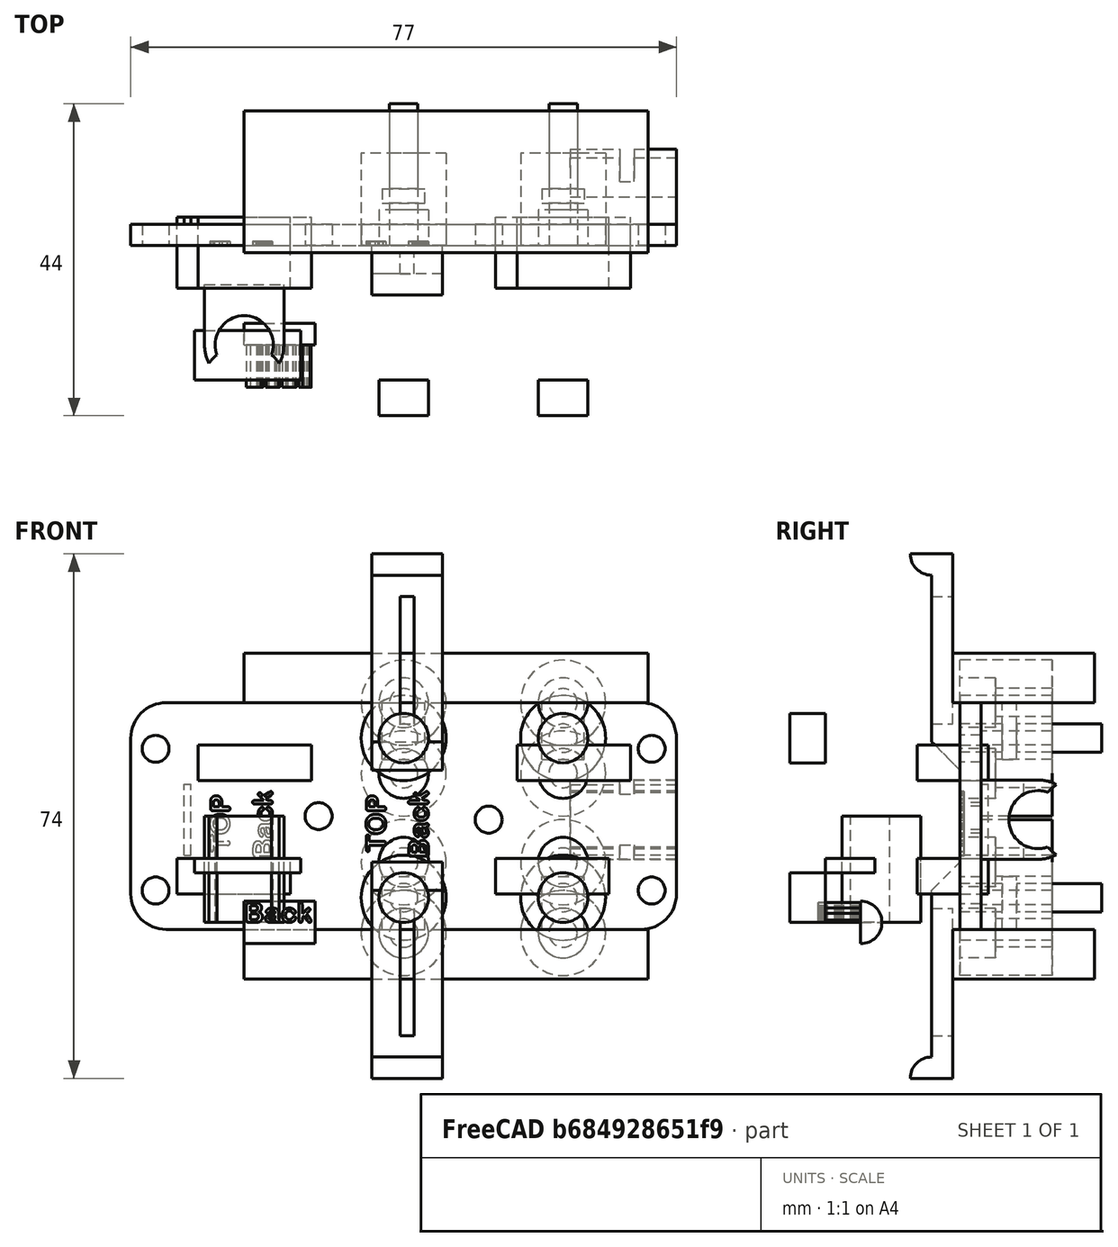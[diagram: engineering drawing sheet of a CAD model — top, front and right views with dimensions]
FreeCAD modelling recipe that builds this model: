
FCSTD DOCUMENT  (FreeCAD 0.16R6712 (Git))
Label: ParkingTransportPlate
License: All rights reserved
LicenseURL: http://en.wikipedia.org/wiki/All_rights_reserved
objects: Part::Cylinder×56, Part::MultiFuse×31, Part::Box×23, Part::Cut×19, Part::Feature×12, Part::Part2DObjectPython×2, Part::Extrusion×1
note: 144 computed .brp shape members not serialized (recipe doc carries the construction recipe); baked Part::Feature solids carry a one-line shape summary decoded from their .brp

FEATURE [Part::Part2DObjectPython] ShapeString002  # Draft 2D object (typed FeaturePython)
  FontFile = <path>
  Size = 3
  String = TOP
  Tracking = 4
FEATURE [Part::Feature] Extrude001002001  label="Extrude001003"
  Placement = pos=(18,0,11) rot=(0,-1,0;1.5708rad)
  shape: bbox 2.835 x 6 x 7.877 mm, 76 faces, 3 solids (baked)
FEATURE [Part::Part2DObjectPython] ShapeString003  # Draft 2D object (typed FeaturePython)
  FontFile = <path>
  Size = 3
  String = Back
  Tracking = 4
FEATURE [Part::Extrusion] Extrude001002002
  Base = -> ShapeString003
  Dir = (0,0,6)
  Placement = pos=(0,0,0) rot=(1,0,0;1.5708rad)
  Solid = false
FEATURE [Part::Feature] Extrude001002002001  label="Extrude001002003"
  Placement = pos=(24,0,10) rot=(0,-1,0;1.5708rad)
  shape: bbox 2.835 x 6 x 9.142 mm, 140 faces, 4 solids (baked)
FEATURE [Part::Box] Box035  label="Würfel034"
  Height = 32
  Length = 77
  Placement = pos=(-16,14,-1) rot=(0,0,1;0rad)
  Width = 3
FEATURE [Part::MultiFuse] Fusion  label="Label"
  Placement = pos=(-20,14.6,-1) rot=(0,0,1;0rad)
  Shapes = -> [Extrude001002002001,Extrude001002001]
FEATURE [Part::Cut] Cut
  Base = -> Box035
  Tool = -> Fusion
FEATURE [Part::Box] Box  label="Würfel"
  Height = 21
  Length = 10
  Placement = pos=(0,0,-2) rot=(0,0,1;0rad)
  Width = 3
FEATURE [Part::Cylinder] Cylinder  label="Zylinder"
  Angle = 180
  Height = 10
  Placement = pos=(0,0,0) rot=(0,1,0;1.5708rad)
  Radius = 3
FEATURE [Part::Feature] Cylinder040  label="Zylinder031"
  Placement = pos=(0,0,-2) rot=(1,0,0;1.5708rad)
  shape: bbox 10 x 6 x 3 mm, 4 faces (baked)
FEATURE [Part::MultiFuse] Fusion026006
  Placement = pos=(18,10,-20) rot=(0,0,1;0rad)
  Shapes = -> [Box,Cylinder040]
FEATURE [Part::Box] Box036  label="Würfel035"
  Height = 21
  Length = 10
  Placement = pos=(0,0,-2) rot=(0,0,1;0rad)
  Width = 3
FEATURE [Part::Feature] Cylinder041  label="Zylinder032"
  Placement = pos=(0,0,-2) rot=(1,0,0;1.5708rad)
  shape: bbox 10 x 6 x 3 mm, 4 faces (baked)
FEATURE [Part::MultiFuse] Fusion026007
  Placement = pos=(28,10,50) rot=(0,1,0;3.14159rad)
  Shapes = -> [Box036,Cylinder041]
FEATURE [Part::Cylinder] Cylinder051  label="Zylinder042"
  Angle = 90
  Height = 40
  Placement = pos=(33,25,29) rot=(1,0,0;1.5708rad)
  Radius = 8
FEATURE [Part::Cylinder] Cylinder052  label="Zylinder043"
  Angle = 90
  Height = 40
  Placement = pos=(33,25,29) rot=(1,0,0;1.5708rad)
  Radius = 5
FEATURE [Part::Cut] Cut011004004
  Base = -> Cylinder051
  Placement = pos=(18,0,-7) rot=(0,-1,0;1.5708rad)
  Tool = -> Cylinder052
FEATURE [Part::Cylinder] Cylinder053  label="Zylinder044"
  Angle = 90
  Height = 40
  Placement = pos=(33,25,29) rot=(1,0,0;1.5708rad)
  Radius = 8
FEATURE [Part::Cylinder] Cylinder054  label="Zylinder045"
  Angle = 90
  Height = 40
  Placement = pos=(33,25,29) rot=(1,0,0;1.5708rad)
  Radius = 5
FEATURE [Part::Cut] Cut011004005
  Base = -> Cylinder053
  Placement = pos=(22,0,33) rot=(0,1,0;3.14159rad)
  Tool = -> Cylinder054
FEATURE [Part::Cylinder] Cylinder055  label="Zylinder046"
  Angle = 90
  Height = 40
  Placement = pos=(33,25,29) rot=(1,0,0;1.5708rad)
  Radius = 8
FEATURE [Part::Cylinder] Cylinder056  label="Zylinder047"
  Angle = 90
  Height = 40
  Placement = pos=(33,25,29) rot=(1,0,0;1.5708rad)
  Radius = 5
FEATURE [Part::Cut] Cut011004006
  Base = -> Cylinder055
  Placement = pos=(23,0,-3) rot=(0,0,1;0rad)
  Tool = -> Cylinder056
FEATURE [Part::Cylinder] Cylinder059  label="Zylinder050"
  Angle = 90
  Height = 40
  Placement = pos=(33,25,29) rot=(1,0,0;1.5708rad)
  Radius = 8
FEATURE [Part::Cylinder] Cylinder060  label="Zylinder051"
  Angle = 90
  Height = 40
  Placement = pos=(33,25,29) rot=(1,0,0;1.5708rad)
  Radius = 5
FEATURE [Part::Cut] Cut011004008
  Base = -> Cylinder059
  Placement = pos=(27,0,37) rot=(0,1,0;1.5708rad)
  Tool = -> Cylinder060
FEATURE [Part::MultiFuse] Fusion026012  label="RoundEdges"
  Shapes = -> [Cut011004008,Cut011004006,Cut011004004,Cut011004005]
FEATURE [Part::Box] Box037  label="Würfel036"
  Height = 10
  Length = 10
  Width = 4
FEATURE [Part::Box] Box038  label="Würfel037"
  Height = 10
  Length = 10
  Placement = pos=(0,-5,9) rot=(-1,0,0;0.785398rad)
  Width = 6
FEATURE [Part::Cut] Cut011004009
  Base = -> Box037
  Placement = pos=(18,10,-1) rot=(0,0,1;0rad)
  Tool = -> Box038
FEATURE [Part::Box] Box039  label="Würfel038"
  Height = 10
  Length = 10
  Width = 4
FEATURE [Part::Box] Box040  label="Würfel039"
  Height = 10
  Length = 10
  Placement = pos=(0,-5,9) rot=(-1,0,0;0.785398rad)
  Width = 6
FEATURE [Part::Cut] Cut011004010
  Base = -> Box039
  Placement = pos=(28,10,31) rot=(0,1,0;3.14159rad)
  Tool = -> Box040
FEATURE [Part::Box] Box041  label="Würfel040"
  Height = 18
  Length = 2
  Placement = pos=(22,-1,-16) rot=(0,0,1;0rad)
  Width = 14
FEATURE [Part::Box] Box042  label="Würfel041"
  Height = 18
  Length = 2
  Placement = pos=(22,-1,28) rot=(0,0,1;0rad)
  Width = 14
FEATURE [Part::MultiFuse] Fusion026013
  Shapes = -> [Fusion026007,Cut011004010]
FEATURE [Part::Cut] Cut011004011  label="DecuplerLeft"
  Base = -> Fusion026013
  Tool = -> Box042
FEATURE [Part::MultiFuse] Fusion026014
  Shapes = -> [Fusion026006,Cut011004009]
FEATURE [Part::Cut] Cut011004012  label="DecuplerRight"
  Base = -> Fusion026014
  Tool = -> Box041
FEATURE [Part::Cylinder] Cylinder034  label="Zylinder025"
  Angle = 360
  Height = 26
  Placement = pos=(-13,16,4.5) rot=(1,0,0;1.5708rad)
  Radius = 1.9
FEATURE [Part::Cylinder] Cylinder035  label="Zylinder026"
  Angle = 360
  Height = 26
  Placement = pos=(-13,16,24.5) rot=(1,0,0;1.5708rad)
  Radius = 1.9
FEATURE [Part::Cylinder] Cylinder036  label="Zylinder027"
  Angle = 360
  Height = 26
  Placement = pos=(10.5,16,15) rot=(1,0,0;1.5708rad)
  Radius = 1.9
FEATURE [Part::MultiFuse] Fusion026003
  Placement = pos=(0.5,0,0) rot=(0,0,1;0rad)
  Shapes = -> [Cylinder034,Cylinder035]
FEATURE [Part::Cylinder] Cylinder037  label="Zylinder028"
  Angle = 360
  Height = 26
  Placement = pos=(-13,16,4.5) rot=(1,0,0;1.5708rad)
  Radius = 1.9
FEATURE [Part::Cylinder] Cylinder038  label="Zylinder029"
  Angle = 360
  Height = 26
  Placement = pos=(-13,16,24.5) rot=(1,0,0;1.5708rad)
  Radius = 1.9
FEATURE [Part::MultiFuse] Fusion026004
  Placement = pos=(70.5,0,0) rot=(0,0,1;0rad)
  Shapes = -> [Cylinder037,Cylinder038]
FEATURE [Part::Cylinder] Cylinder039  label="Zylinder030"
  Angle = 360
  Height = 26
  Placement = pos=(34.5,16,14.5) rot=(1,0,0;1.5708rad)
  Radius = 1.9
FEATURE [Part::MultiFuse] Fusion026005  label="Bohrung"
  Placement = pos=(0,3,0) rot=(0,0,1;0rad)
  Shapes = -> [Cylinder036,Fusion026003,Fusion026004,Cylinder039]
FEATURE [Part::MultiFuse] Fusion026015
  Shapes = -> [Fusion026012,Fusion026005]
FEATURE [Part::Cut] Cut011004013  label="BasePlate"
  Base = -> Cut
  Tool = -> Fusion026015
FEATURE [Part::Box] Box034  label="Würfel033"
  Height = 5
  Length = 16
  Placement = pos=(-9.5,-18,4) rot=(0,0,1;0rad)
  Width = 10
FEATURE [Part::Box] Box043  label="Würfel042"
  Height = 5
  Length = 16
  Placement = pos=(35.5,-18,4) rot=(0,0,1;0rad)
  Width = 10
FEATURE [Part::Box] Box044  label="Würfel043"
  Height = 5
  Length = 16
  Placement = pos=(-6.5,-18,20) rot=(0,0,1;0rad)
  Width = 10
FEATURE [Part::Box] Box045  label="Würfel044"
  Height = 5
  Length = 16
  Placement = pos=(38.5,-18,20) rot=(0,0,1;0rad)
  Width = 10
FEATURE [Part::MultiFuse] Fusion026017  label="SripperHoles"
  Placement = pos=(0,26,0) rot=(0,0,1;0rad)
  Shapes = -> [Box034,Box045,Box043,Box044]
FEATURE [Part::Feature] Cut011004014001  label="BasePlateOpen_export"
  shape: bbox 77 x 3 x 32 mm, 246 faces (baked)
FEATURE [Part::Feature] Cut011004013001  label="BasePlate_export"
  shape: bbox 77 x 3 x 32 mm, 230 faces (baked)
FEATURE [Part::Cylinder] Cylinder061  label="Zylinder052"
  Angle = 360
  Height = 20
  Placement = pos=(-3.5,14,0) rot=(0,0,1;0rad)
  Radius = 2
FEATURE [Part::Cylinder] Cylinder001  label="Zylinder001"
  Angle = 360
  Height = 20
  Placement = pos=(-3.5,36.5,0) rot=(0,0,1;0rad)
  Radius = 2
FEATURE [Part::Cylinder] Cylinder002  label="Zylinder002"
  Angle = 360
  Height = 20
  Placement = pos=(19,14,0) rot=(0,0,1;0rad)
  Radius = 2
FEATURE [Part::Cylinder] Cylinder003  label="Zylinder003"
  Angle = 360
  Height = 20
  Placement = pos=(19,36.5,0) rot=(0,0,1;0rad)
  Radius = 2
FEATURE [Part::MultiFuse] Fusion026018
  Placement = pos=(26,10,-10.5) rot=(1,0,0;1.5708rad)
  Shapes = -> [Cylinder061,Cylinder002,Cylinder003,Cylinder001]
FEATURE [Part::Cylinder] Cylinder062  label="Zylinder053"
  Angle = 360
  Height = 5
  Placement = pos=(-3.5,14,0) rot=(0,0,1;0rad)
  Radius = 3.5
FEATURE [Part::Cylinder] Cylinder063  label="Zylinder054"
  Angle = 360
  Height = 5
  Placement = pos=(-3.5,36.5,0) rot=(0,0,1;0rad)
  Radius = 3.5
FEATURE [Part::Cylinder] Cylinder064  label="Zylinder055"
  Angle = 360
  Height = 5
  Placement = pos=(19,14,0) rot=(0,0,1;0rad)
  Radius = 3.5
FEATURE [Part::Cylinder] Cylinder065  label="Zylinder056"
  Angle = 360
  Height = 5
  Placement = pos=(19,36.5,0) rot=(0,0,1;0rad)
  Radius = 3.5
FEATURE [Part::MultiFuse] Fusion026019
  Placement = pos=(26,-5,-10.5) rot=(1,0,0;1.5708rad)
  Shapes = -> [Cylinder062,Cylinder064,Cylinder065,Cylinder063]
FEATURE [Part::Cylinder] Cylinder066  label="Zylinder057"
  Angle = 360
  Height = 13
  Placement = pos=(-3.5,14,0) rot=(0,0,1;0rad)
  Radius = 6
FEATURE [Part::Cylinder] Cylinder067  label="Zylinder058"
  Angle = 360
  Height = 13
  Placement = pos=(-3.5,36.5,0) rot=(0,0,1;0rad)
  Radius = 6
FEATURE [Part::Cylinder] Cylinder068  label="Zylinder059"
  Angle = 360
  Height = 13
  Placement = pos=(19,14,0) rot=(0,0,1;0rad)
  Radius = 6
FEATURE [Part::Cylinder] Cylinder069  label="Zylinder060"
  Angle = 360
  Height = 13
  Placement = pos=(19,36.5,0) rot=(0,0,1;0rad)
  Radius = 6
FEATURE [Part::MultiFuse] Fusion026020  label="E3DV6Mount_Base"
  Placement = pos=(26,27,-15.5) rot=(1,0,0;1.5708rad)
  Shapes = -> [Cylinder066,Cylinder068,Cylinder069,Cylinder067]
FEATURE [Part::MultiFuse] Fusion026021  label="E3DV6Mount_Bohrung"
  Placement = pos=(0,24,-5) rot=(0,0,1;0rad)
  Shapes = -> [Fusion026018,Fusion026019]
FEATURE [Part::MultiFuse] Fusion026022  label="E3DV6Mount_Full"
  Shapes = -> [Fusion026020,Cut011004013]
FEATURE [Part::Cut] Cut011004014002  label="E3DV6Mount"
  Base = -> Fusion026022
  Tool = -> Fusion026021
FEATURE [Part::Feature] Cut011004014002001  label="E3DV6Mount001"
  shape: bbox 77 x 13 x 38 mm, 252 faces (baked)
FEATURE [Part::Feature] Cut011004014002002  label="E3DV6Mount002"
  shape: bbox 77 x 13 x 38.5 mm, 252 faces (baked)
FEATURE [Part::Feature] Extrude001002002002  label="Extrude001002002004"
  Placement = pos=(18,0,11) rot=(0,-1,0;1.5708rad)
  shape: bbox 2.835 x 6 x 7.877 mm, 76 faces, 3 solids (baked)
FEATURE [Part::Feature] Extrude001002002003  label="Extrude001002002005"
  Placement = pos=(24,0,10) rot=(0,-1,0;1.5708rad)
  shape: bbox 2.835 x 6 x 9.142 mm, 140 faces, 4 solids (baked)
FEATURE [Part::Box] Box046  label="Würfel045"
  Height = 32
  Length = 77
  Placement = pos=(-16,14,-1) rot=(0,0,1;0rad)
  Width = 3
FEATURE [Part::MultiFuse] Fusion026023  label="Label001"
  Placement = pos=(-20,14.6,-1) rot=(0,0,1;0rad)
  Shapes = -> [Extrude001002002003,Extrude001002002002]
FEATURE [Part::Cut] Cut011004014002003
  Base = -> Box046
  Tool = -> Fusion026023
FEATURE [Part::Cylinder] Cylinder070  label="Zylinder061"
  Angle = 90
  Height = 40
  Placement = pos=(33,25,29) rot=(1,0,0;1.5708rad)
  Radius = 8
FEATURE [Part::Cylinder] Cylinder071  label="Zylinder062"
  Angle = 90
  Height = 40
  Placement = pos=(33,25,29) rot=(1,0,0;1.5708rad)
  Radius = 5
FEATURE [Part::Cut] Cut011004014002004
  Base = -> Cylinder070
  Placement = pos=(18,0,-7) rot=(0,-1,0;1.5708rad)
  Tool = -> Cylinder071
FEATURE [Part::Cylinder] Cylinder072  label="Zylinder063"
  Angle = 90
  Height = 40
  Placement = pos=(33,25,29) rot=(1,0,0;1.5708rad)
  Radius = 8
FEATURE [Part::Cylinder] Cylinder073  label="Zylinder064"
  Angle = 90
  Height = 40
  Placement = pos=(33,25,29) rot=(1,0,0;1.5708rad)
  Radius = 5
FEATURE [Part::Cut] Cut011004014002005
  Base = -> Cylinder072
  Placement = pos=(22,0,33) rot=(0,1,0;3.14159rad)
  Tool = -> Cylinder073
FEATURE [Part::Cylinder] Cylinder074  label="Zylinder065"
  Angle = 90
  Height = 40
  Placement = pos=(33,25,29) rot=(1,0,0;1.5708rad)
  Radius = 8
FEATURE [Part::Cylinder] Cylinder075  label="Zylinder066"
  Angle = 90
  Height = 40
  Placement = pos=(33,25,29) rot=(1,0,0;1.5708rad)
  Radius = 5
FEATURE [Part::Cut] Cut011004014002006
  Base = -> Cylinder074
  Placement = pos=(23,0,-3) rot=(0,0,1;0rad)
  Tool = -> Cylinder075
FEATURE [Part::Cylinder] Cylinder076  label="Zylinder067"
  Angle = 90
  Height = 40
  Placement = pos=(33,25,29) rot=(1,0,0;1.5708rad)
  Radius = 8
FEATURE [Part::Cylinder] Cylinder077  label="Zylinder068"
  Angle = 90
  Height = 40
  Placement = pos=(33,25,29) rot=(1,0,0;1.5708rad)
  Radius = 5
FEATURE [Part::Cut] Cut011004014002007
  Base = -> Cylinder076
  Placement = pos=(27,0,37) rot=(0,1,0;1.5708rad)
  Tool = -> Cylinder077
FEATURE [Part::MultiFuse] Fusion026024  label="RoundEdges001"
  Shapes = -> [Cut011004014002007,Cut011004014002006,Cut011004014002004,Cut011004014002005]
FEATURE [Part::Cylinder] Cylinder078  label="Zylinder069"
  Angle = 360
  Height = 26
  Placement = pos=(-13,16,4.5) rot=(1,0,0;1.5708rad)
  Radius = 1.9
FEATURE [Part::Cylinder] Cylinder079  label="Zylinder070"
  Angle = 360
  Height = 26
  Placement = pos=(-13,16,24.5) rot=(1,0,0;1.5708rad)
  Radius = 1.9
FEATURE [Part::Cylinder] Cylinder080  label="Zylinder071"
  Angle = 360
  Height = 26
  Placement = pos=(10.5,16,15) rot=(1,0,0;1.5708rad)
  Radius = 1.9
FEATURE [Part::MultiFuse] Fusion026025
  Placement = pos=(0.5,0,0) rot=(0,0,1;0rad)
  Shapes = -> [Cylinder078,Cylinder079]
FEATURE [Part::Cylinder] Cylinder081  label="Zylinder072"
  Angle = 360
  Height = 26
  Placement = pos=(-13,16,4.5) rot=(1,0,0;1.5708rad)
  Radius = 1.9
FEATURE [Part::Cylinder] Cylinder082  label="Zylinder073"
  Angle = 360
  Height = 26
  Placement = pos=(-13,16,24.5) rot=(1,0,0;1.5708rad)
  Radius = 1.9
FEATURE [Part::MultiFuse] Fusion026026
  Placement = pos=(70.5,0,0) rot=(0,0,1;0rad)
  Shapes = -> [Cylinder081,Cylinder082]
FEATURE [Part::Cylinder] Cylinder083  label="Zylinder074"
  Angle = 360
  Height = 26
  Placement = pos=(34.5,16,14.5) rot=(1,0,0;1.5708rad)
  Radius = 1.9
FEATURE [Part::MultiFuse] Fusion026027  label="Bohrung001"
  Placement = pos=(0,3,0) rot=(0,0,1;0rad)
  Shapes = -> [Cylinder080,Fusion026025,Fusion026026,Cylinder083]
FEATURE [Part::MultiFuse] Fusion026028
  Shapes = -> [Fusion026024,Fusion026027]
FEATURE [Part::Cut] Cut011004014002008  label="BasePlate001"
  Base = -> Cut011004014002003
  Tool = -> Fusion026028
FEATURE [Part::Cylinder] Cylinder084  label="Zylinder075"
  Angle = 360
  Height = 20
  Placement = pos=(-3.5,14,0) rot=(0,0,1;0rad)
  Radius = 2
FEATURE [Part::Cylinder] Cylinder085  label="Zylinder076"
  Angle = 360
  Height = 20
  Placement = pos=(-3.5,36.5,0) rot=(0,0,1;0rad)
  Radius = 2
FEATURE [Part::Cylinder] Cylinder086  label="Zylinder077"
  Angle = 360
  Height = 20
  Placement = pos=(19,14,0) rot=(0,0,1;0rad)
  Radius = 2
FEATURE [Part::Cylinder] Cylinder087  label="Zylinder078"
  Angle = 360
  Height = 20
  Placement = pos=(19,36.5,0) rot=(0,0,1;0rad)
  Radius = 2
FEATURE [Part::MultiFuse] Fusion026029  label="Bohrloch"
  Placement = pos=(26,10,-10.5) rot=(1,0,0;1.5708rad)
  Shapes = -> [Cylinder084,Cylinder086,Cylinder087,Cylinder085]
FEATURE [Part::Cylinder] Cylinder088  label="Zylinder079"
  Angle = 360
  Height = 5
  Placement = pos=(-3.5,14,0) rot=(0,0,1;0rad)
  Radius = 3.5
FEATURE [Part::Cylinder] Cylinder089  label="Zylinder080"
  Angle = 360
  Height = 5
  Placement = pos=(-3.5,36.5,0) rot=(0,0,1;0rad)
  Radius = 3.5
FEATURE [Part::Cylinder] Cylinder090  label="Zylinder081"
  Angle = 360
  Height = 5
  Placement = pos=(19,14,0) rot=(0,0,1;0rad)
  Radius = 3.5
FEATURE [Part::Cylinder] Cylinder091  label="Zylinder082"
  Angle = 360
  Height = 5
  Placement = pos=(19,36.5,0) rot=(0,0,1;0rad)
  Radius = 3.5
FEATURE [Part::MultiFuse] Fusion026030  label="MutterSenke"
  Placement = pos=(26,-5,-10.5) rot=(1,0,0;1.5708rad)
  Shapes = -> [Cylinder088,Cylinder090,Cylinder091,Cylinder089]
FEATURE [Part::Cylinder] Cylinder092  label="Zylinder083"
  Angle = 360
  Height = 13
  Placement = pos=(-3.5,14,0) rot=(0,0,1;0rad)
  Radius = 6
FEATURE [Part::Cylinder] Cylinder093  label="Zylinder084"
  Angle = 360
  Height = 13
  Placement = pos=(-3.5,36.5,0) rot=(0,0,1;0rad)
  Radius = 6
FEATURE [Part::Cylinder] Cylinder094  label="Zylinder085"
  Angle = 360
  Height = 13
  Placement = pos=(19,14,0) rot=(0,0,1;0rad)
  Radius = 6
FEATURE [Part::Cylinder] Cylinder095  label="Zylinder086"
  Angle = 360
  Height = 13
  Placement = pos=(19,36.5,0) rot=(0,0,1;0rad)
  Radius = 6
FEATURE [Part::MultiFuse] Fusion026031  label="E3DV6Mount_Base001"
  Placement = pos=(26,27,-10.5) rot=(1,0,0;1.5708rad)
  Shapes = -> [Cylinder092,Cylinder094,Cylinder095,Cylinder093]
FEATURE [Part::Box] Box047  label="Würfel046"
  Height = 12
  Length = 6
  Placement = pos=(19.5,-4,23) rot=(0,0,1;0rad)
  Width = 2
FEATURE [Part::Box] Box048  label="Würfel047"
  Height = 12
  Length = 6
  Placement = pos=(42,-4,-5.5) rot=(0,0,1;0rad)
  Width = 2
FEATURE [Part::Box] Box049  label="Würfel048"
  Height = 12
  Length = 6
  Placement = pos=(19.5,-4,-5.5) rot=(0,0,1;0rad)
  Width = 2
FEATURE [Part::Box] Box050  label="Würfel049"
  Height = 12
  Length = 6
  Placement = pos=(42,-4,23) rot=(0,0,1;0rad)
  Width = 2
FEATURE [Part::MultiFuse] Fusion026034  label="MutterSchlitz"
  Shapes = -> [Box047,Box048,Box049,Box050]
FEATURE [Part::MultiFuse] Fusion026035  label="Bohrung002"
  Placement = pos=(0,24,0) rot=(0,0,1;0rad)
  Shapes = -> [Fusion026029,Fusion026034]
FEATURE [Part::Box] Box051  label="Würfel050"
  Height = 7
  Length = 57
  Placement = pos=(0,13,-8) rot=(0,0,1;0rad)
  Width = 20
FEATURE [Part::Box] Box052  label="Würfel051"
  Height = 7
  Length = 57
  Placement = pos=(0,13,31) rot=(0,0,1;0rad)
  Width = 20
FEATURE [Part::MultiFuse] Fusion026036  label="SideCut"
  Shapes = -> [Box051,Box052]
FEATURE [Part::MultiFuse] Fusion026037  label="fullCut"
  Shapes = -> [Fusion026035,Fusion026036]
FEATURE [Part::Cylinder] Cylinder096  label="Zylinder087"
  Angle = 360
  Height = 15
  Radius = 4.1
FEATURE [Part::Cylinder] Cylinder097  label="Zylinder088"
  Angle = 360
  Height = 15
  Radius = 5.6
FEATURE [Part::Box] Box053  label="Würfel052"
  Height = 15
  Length = 11.2
  Placement = pos=(-5.6,0,0) rot=(0,0,1;0rad)
  Width = 8.5
FEATURE [Part::MultiFuse] Fusion026038
  Shapes = -> [Cylinder097,Box053]
FEATURE [Part::Cut] Cut011004014002010
  Base = -> Fusion026038
  Tool = -> Cylinder096
FEATURE [Part::Cylinder] Cylinder098  label="Zylinder089"
  Angle = 360
  Height = 15
  Placement = pos=(0,-6,0) rot=(0,0,1;0rad)
  Radius = 6
FEATURE [Part::Cut] Cut011004014002011
  Base = -> Cut011004014002010
  Tool = -> Cylinder098
FEATURE [Part::Box] Box054  label="Würfel053"
  Height = 2
  Length = 15
  Placement = pos=(-7,-5,7) rot=(0,0,1;0rad)
  Width = 7
FEATURE [Part::Feature] Cut011004014002012001  label="Cut011004014002013"
  Placement = pos=(46,25,14.5) rot=(0,1,0;1.5708rad)
  shape: bbox 15 x 11.11 x 11.2 mm, 20 faces (baked)
FEATURE [Part::Box] Box055  label="Würfel054"
  Height = 10
  Length = 1
  Placement = pos=(-8.5,17,9.5) rot=(0,0,1;0rad)
  Width = 1
FEATURE [Part::MultiFuse] Fusion026039  label="TransportBladeGauge"
  Shapes = -> [Cut011004014002012001,Box055,Cut011004014002008]
FEATURE [Part::Feature] Fusion026039001  label="TransportBladeGauge001"
  shape: bbox 77 x 13.61 x 32 mm, 253 faces (baked)
note: 2 file-system paths scrubbed to <path> (originals preserved in the JSON sidecar)
